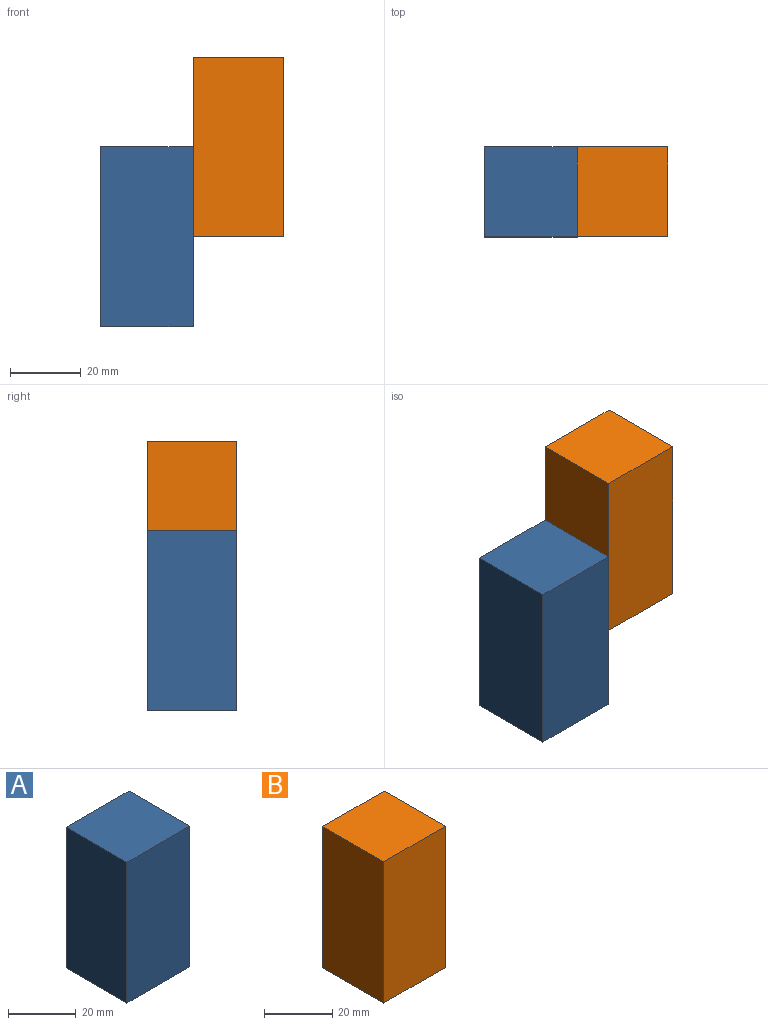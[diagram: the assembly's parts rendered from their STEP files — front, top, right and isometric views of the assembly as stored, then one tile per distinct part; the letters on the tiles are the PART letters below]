
ASSEMBLY  parts=2 mates=1
PART A: 6 faces, bbox 26.3x25.4x51 mm
  f0: plane 26.28x25.4mm, normal (0,0,1), area 667.5mm2, adj f1,f3,f4,f5
  f1: plane 51.01x25.4mm, normal (-1,0,0), area 1295.6mm2, adj f0,f2,f4,f5
  f2: plane 26.28x25.4mm, normal (0,0,-1), area 667.5mm2, adj f1,f3,f4,f5
  f3: plane 51.01x25.4mm, normal (1,0,0), area 1295.6mm2, adj f0,f2,f4,f5
  f4: plane 51.01x26.28mm, normal (0,-1,0), area 1340.4mm2, adj f0,f1,f2,f3
  f5: plane 51.01x26.28mm, normal (0,1,0), area 1340.4mm2, adj f0,f1,f2,f3
PART B: 6 faces, bbox 25.6x25.4x50.9 mm
  f0: plane 25.57x25.4mm, normal (0,0,1), area 649.4mm2, adj f1,f3,f4,f5
  f1: plane 50.86x25.4mm, normal (-1,0,0), area 1291.8mm2, adj f0,f2,f4,f5
  f2: plane 25.57x25.4mm, normal (0,0,-1), area 649.4mm2, adj f1,f3,f4,f5
  f3: plane 50.86x25.4mm, normal (1,0,0), area 1291.8mm2, adj f0,f2,f4,f5
  f4: plane 50.86x25.57mm, normal (0,-1,0), area 1300.4mm2, adj f0,f1,f2,f3
  f5: plane 50.86x25.57mm, normal (0,1,0), area 1300.4mm2, adj f0,f1,f2,f3
PLACE A t=(20.42,10.82,-1.45)mm
PLACE B t=(13.32,10.82,-10.62)mm
MATE fastened B.f1 <-> A.f3  axis (-1,0,0) through (-74.66,-1.88,24.58)mm
